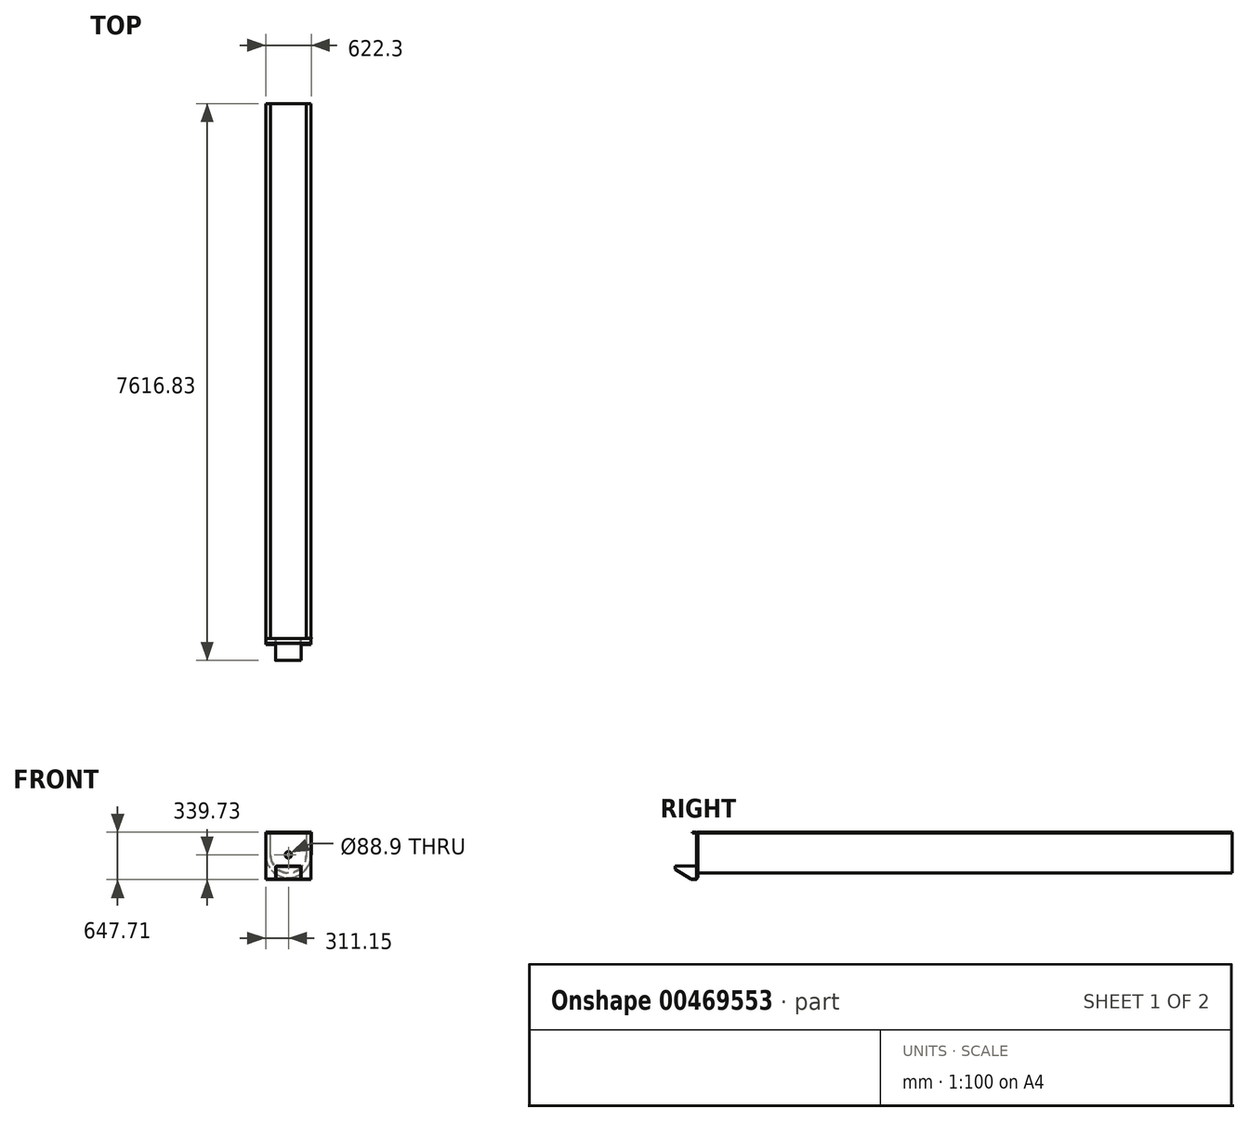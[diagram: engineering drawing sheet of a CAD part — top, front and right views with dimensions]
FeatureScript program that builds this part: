
annotation { "Feature Type Name" : "Feature", "Feature Type Description" : "" }
export const myFeature = defineFeature(function(context is Context, id is Id, definition is map)
    precondition{}
    {
        {
            var Q0;
            Q0=qCreatedBy(makeId("Front.planeOp"),FACE);
            var sketch = newSketch(context, id + "F0", { "sketchPlane" : qUnion([Q0])});
            skArc(sketch, "E0", {"start": v(-241.3, 0) * mm, "mid": v(0, -241.3) * mm, "end": v(241.3, 0) * mm});
            skLineSegment(sketch, "E1", {"start": v(-241.3, 0) * mm, "end": v(-241.3, 307.98) * mm});
            skLineSegment(sketch, "E2", {"start": v(-241.3, 307.98) * mm, "end": v(241.3, 307.98) * mm, "construction": true});
            skLineSegment(sketch, "E3", {"start": v(241.3, 307.98) * mm, "end": v(241.3, 0) * mm});
            skLineSegment(sketch, "E4.0", {"start": v(-250.83, 0) * mm, "end": v(-250.83, 298.45) * mm});
            skArc(sketch, "E4.1", {"start": v(-250.83, 0) * mm, "mid": v(0, -250.83) * mm, "end": v(250.83, 0) * mm});
            skLineSegment(sketch, "E4.2", {"start": v(250.83, 298.45) * mm, "end": v(250.83, 0) * mm});
            skLineSegment(sketch, "E5", {"start": v(-304.8, 307.98) * mm, "end": v(-241.3, 307.98) * mm});
            skLineSegment(sketch, "E6", {"start": v(304.8, 307.98) * mm, "end": v(241.3, 307.98) * mm});
            skLineSegment(sketch, "E7", {"start": v(-250.83, 298.45) * mm, "end": v(-304.8, 298.45) * mm});
            skLineSegment(sketch, "E8", {"start": v(-304.8, 298.45) * mm, "end": v(-304.8, 307.98) * mm});
            skLineSegment(sketch, "E9", {"start": v(250.83, 298.45) * mm, "end": v(304.8, 298.45) * mm});
            skLineSegment(sketch, "E10", {"start": v(304.8, 298.45) * mm, "end": v(304.8, 307.98) * mm});
            skSolve(sketch);
        }
        {
            var Q0;
            Q0=makeQuery(id+"F0.imprint","IMPRINT",FACE,{"disambiguationData":[TD([[makeQuery(id+"F0.imprint","IMPRINT",EDGE,{"derivedFrom":sQuery(id+"F0.wireOp",EDGE,"E0")}),-1.0]])]});
            extrude(context, id + "F1", {"entities" : qUnion([Q0]), "oppositeDirection" : true, "depth" : 7315.2 * mm});
        }
        {
            var Q0;
            Q0=qCreatedBy(makeId("Front.planeOp"),FACE);
            var sketch = newSketch(context, id + "F2", { "sketchPlane" : qUnion([Q0])});
            skLineSegment(sketch, "E11", {"start": v(-247.65, 307.98) * mm, "end": v(247.65, 307.98) * mm, "construction": true});
            skLineSegment(sketch, "E12", {"start": v(-247.65, 307.98) * mm, "end": v(-311.15, 307.98) * mm});
            skLineSegment(sketch, "E13", {"start": v(247.65, 307.98) * mm, "end": v(311.15, 307.98) * mm});
            skLineSegment(sketch, "E14", {"start": v(311.15, 307.98) * mm, "end": v(311.15, 0) * mm});
            skLineSegment(sketch, "E15", {"start": v(-311.15, 307.98) * mm, "end": v(-311.15, 0) * mm});
            skArc(sketch, "E16", {"start": v(-247.65, 0) * mm, "mid": v(0, -247.65) * mm, "end": v(247.65, 0) * mm});
            skArc(sketch, "E17", {"start": v(-311.15, 0) * mm, "mid": v(0, -311.15) * mm, "end": v(311.15, 0) * mm});
            skLineSegment(sketch, "E18", {"start": v(-247.65, 307.98) * mm, "end": v(-247.65, 0) * mm});
            skLineSegment(sketch, "E19", {"start": v(247.65, 307.98) * mm, "end": v(247.65, 0) * mm});
            skSolve(sketch);
        }
        {
            var Q0;
            Q0 = qSketchRegion(id + "F2", true);
            extrude(context, id + "F3", {"entities" : qUnion([Q0]), "operationType" : NewBodyOperationType.ADD, "oppositeDirection" : true, "depth" : 9.52 * mm});
        }
        {
            var Q0;
            Q0=qCreatedBy(makeId("Right.planeOp"),FACE);
            var sketch = newSketch(context, id + "F4", { "sketchPlane" : qUnion([Q0])});
            skLineSegment(sketch, "E20", {"start": v(0, 288.93) * mm, "end": v(0, -320.68) * mm});
            skLineSegment(sketch, "E21", {"start": v(-19.05, -339.73) * mm, "end": v(-82.55, -339.73) * mm});
            skLineSegment(sketch, "E22", {"start": v(-82.55, -339.73) * mm, "end": v(-82.55, -330.2) * mm});
            skLineSegment(sketch, "E23", {"start": v(-82.55, -330.2) * mm, "end": v(-19.05, -330.2) * mm});
            skLineSegment(sketch, "E24", {"start": v(-9.52, -320.68) * mm, "end": v(-9.53, 288.93) * mm});
            skLineSegment(sketch, "E25", {"start": v(-19.05, 298.45) * mm, "end": v(-63.5, 298.45) * mm});
            skLineSegment(sketch, "E26", {"start": v(-63.5, 298.45) * mm, "end": v(-63.5, 307.98) * mm});
            skLineSegment(sketch, "E27", {"start": v(-63.5, 307.98) * mm, "end": v(-19.05, 307.98) * mm});
            skLineSegment(sketch, "E28", {"start": v(0, 0) * mm, "end": v(-9.52, 0) * mm, "construction": true});
            skPoint(sketch, "E29.visualSharp", {"position": v(0, 307.98) * mm});
            skArc(sketch, "E29.filletArc", {"start": v(0, 288.93) * mm, "mid": v(-5.58, 302.4) * mm, "end": v(-19.05, 307.98) * mm});
            skPoint(sketch, "E30.visualSharp", {"position": v(0, -339.73) * mm});
            skArc(sketch, "E30.filletArc", {"start": v(-19.05, -339.73) * mm, "mid": v(-5.58, -334.15) * mm, "end": v(0, -320.68) * mm});
            skPoint(sketch, "E31.visualSharp", {"position": v(-9.53, 298.45) * mm});
            skArc(sketch, "E31.filletArc", {"start": v(-9.53, 288.93) * mm, "mid": v(-12.31, 295.66) * mm, "end": v(-19.05, 298.45) * mm});
            skPoint(sketch, "E32.visualSharp", {"position": v(-9.52, -330.2) * mm});
            skArc(sketch, "E32.filletArc", {"start": v(-19.05, -330.2) * mm, "mid": v(-12.31, -327.41) * mm, "end": v(-9.52, -320.68) * mm});
            skSolve(sketch);
        }
        {
            var Q0;
            Q0 = qSketchRegion(id + "F4", true);
            extrude(context, id + "F5", {"entities" : qUnion([Q0]), "operationType" : NewBodyOperationType.ADD, "endBound" : BoundingType.SYMMETRIC, "depth" : 615.95 * mm});
        }
        {
            var Q0;
            Q0=makeQuery(id+"F5.opExtrude","SWEPT_FACE",FACE,{"disambiguationData":[OSD([sQuery(id+"F4.wireOp",EDGE,"E24")])]});
            var sketch = newSketch(context, id + "F6", { "sketchPlane" : qUnion([Q0])});
            skCircle(sketch, "E33", {"center": v(0, 0) * mm, "radius": 44.45 * mm});
            skSolve(sketch);
        }
        {
            var Q0;
            Q0 = qSketchRegion(id + "F6", true);
            extrude(context, id + "F7", {"entities" : qUnion([Q0]), "operationType" : NewBodyOperationType.REMOVE, "endBound" : BoundingType.UP_TO_NEXT, "oppositeDirection" : true, "depth" : 25.4 * mm});
        }
        {
            var Q0;
            Q0=makeQuery(id+"F5.opExtrude","SWEPT_FACE",FACE,{"disambiguationData":[OSD([sQuery(id+"F4.wireOp",EDGE,"E24")])]});
            var sketch = newSketch(context, id + "F8", { "sketchPlane" : qUnion([Q0])});
            skLineSegment(sketch, "E34", {"start": v(-177.8, -330.2) * mm, "end": v(-177.8, -171.45) * mm});
            skLineSegment(sketch, "E35", {"start": v(-158.75, -152.4) * mm, "end": v(158.75, -152.4) * mm});
            skLineSegment(sketch, "E36", {"start": v(177.8, -171.45) * mm, "end": v(177.8, -330.2) * mm});
            skLineSegment(sketch, "E37", {"start": v(177.8, -330.2) * mm, "end": v(168.28, -330.2) * mm});
            skLineSegment(sketch, "E38", {"start": v(168.28, -330.2) * mm, "end": v(168.28, -171.45) * mm});
            skLineSegment(sketch, "E39", {"start": v(158.75, -161.92) * mm, "end": v(-158.75, -161.93) * mm});
            skLineSegment(sketch, "E40", {"start": v(-168.28, -171.45) * mm, "end": v(-168.28, -330.2) * mm});
            skLineSegment(sketch, "E41", {"start": v(-168.28, -330.2) * mm, "end": v(-177.8, -330.2) * mm});
            skLineSegment(sketch, "E42", {"start": v(0, -152.4) * mm, "end": v(0, -161.93) * mm, "construction": true});
            skPoint(sketch, "E43.visualSharp", {"position": v(-168.28, -161.93) * mm});
            skArc(sketch, "E43.filletArc", {"start": v(-158.75, -161.93) * mm, "mid": v(-165.49, -164.71) * mm, "end": v(-168.28, -171.45) * mm});
            skPoint(sketch, "E44.visualSharp", {"position": v(168.28, -161.93) * mm});
            skArc(sketch, "E44.filletArc", {"start": v(168.28, -171.45) * mm, "mid": v(165.49, -164.71) * mm, "end": v(158.75, -161.93) * mm});
            skPoint(sketch, "E45.visualSharp", {"position": v(-177.8, -152.4) * mm});
            skArc(sketch, "E45.filletArc", {"start": v(-158.75, -152.4) * mm, "mid": v(-172.22, -157.98) * mm, "end": v(-177.8, -171.45) * mm});
            skPoint(sketch, "E46.visualSharp", {"position": v(177.8, -152.4) * mm});
            skArc(sketch, "E46.filletArc", {"start": v(177.8, -171.45) * mm, "mid": v(172.22, -157.98) * mm, "end": v(158.75, -152.4) * mm});
            skSolve(sketch);
        }
        {
            var Q0;
            Q0 = qSketchRegion(id + "F8", true);
            extrude(context, id + "F9", {"entities" : qUnion([Q0]), "operationType" : NewBodyOperationType.ADD, "depth" : 292.1 * mm});
        }
        {
            var Q0;
            Q0=makeQuery(id+"F9.opExtrude","SWEPT_FACE",FACE,{"disambiguationData":[OSD([sQuery(id+"F8.wireOp",EDGE,"E36")])]});
            var sketch = newSketch(context, id + "F10", { "sketchPlane" : qUnion([Q0])});
            skLineSegment(sketch, "E47", {"start": v(-82.55, -330.2) * mm, "end": v(-301.63, -196.85) * mm});
            skLineSegment(sketch, "E48", {"start": v(-301.62, -196.85) * mm, "end": v(-301.62, -330.2) * mm});
            skLineSegment(sketch, "E49", {"start": v(-301.62, -330.2) * mm, "end": v(-82.55, -330.2) * mm});
            skSolve(sketch);
        }
        {
            var Q0;
            Q0 = qSketchRegion(id + "F10", true);
            extrude(context, id + "F11", {"entities" : qUnion([Q0]), "operationType" : NewBodyOperationType.REMOVE, "endBound" : BoundingType.THROUGH_ALL, "oppositeDirection" : true, "depth" : 25.4 * mm});
        }
    });
